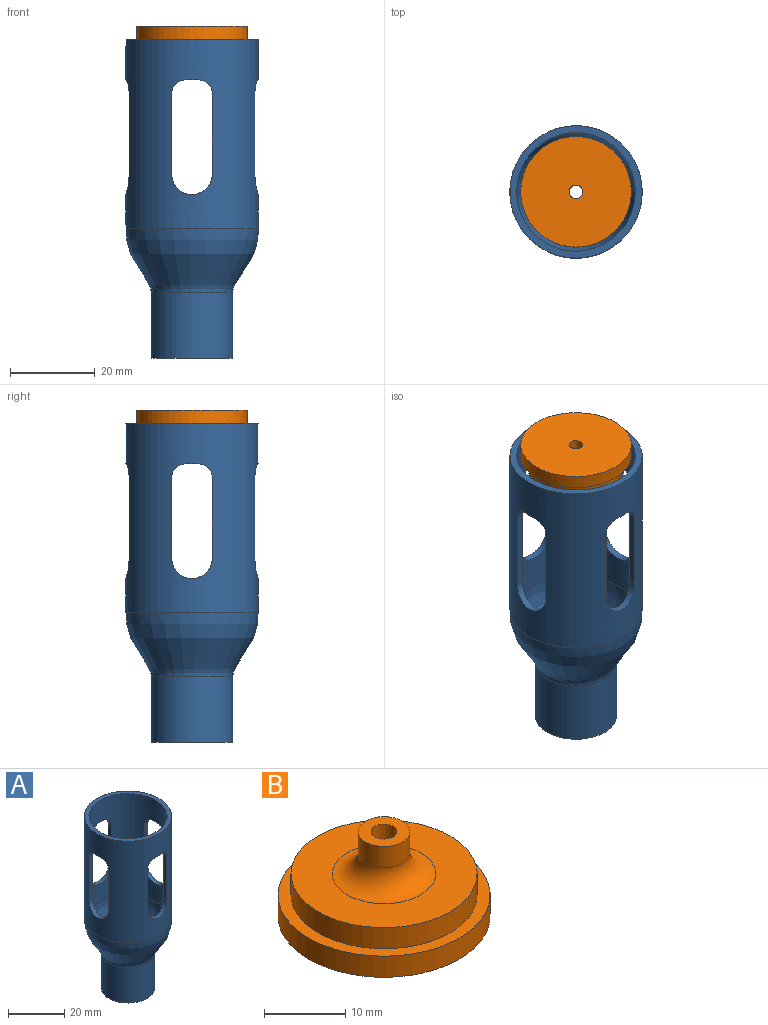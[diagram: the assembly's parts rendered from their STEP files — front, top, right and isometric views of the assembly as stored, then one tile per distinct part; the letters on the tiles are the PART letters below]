
ASSEMBLY  parts=2 mates=1
PART A: 32 faces, bbox 31.1x31.1x75 mm
  f0: cylinder r=13.97mm len=44.48mm, axis (0,0,1), area 2913.2mm2, adj f2,f7,f8,f9,f10,f11,f12,f13
  f1: cylinder r=15.56mm len=44.45mm, axis (0,0,1), area 3358.1mm2, adj f6,f7,f8,f9,f10,f11,f12,f13
  f2: revolved ~27.95x27.95mm, area 1193.1mm2, adj f0,f3
  f3: cylinder r=8mm len=16mm, axis (0,0,1), area 766mm2, adj f2,f4
  f4: plane 19.18x19.18mm, normal (0,0,-1), area 87.7mm2, adj f3,f5
  f5: cylinder r=9.59mm len=19.18mm, axis (0,0,1), area 923.1mm2, adj f4,f6
  f6: revolved ~31.13x31.13mm, area 1371.2mm2, adj f1,f5
  f7: plane 31.12x31.12mm, normal (0,0,1), area 147.3mm2, adj f0,f1
  f8: plane 3.18x1.68mm, normal (0,0,-1), area 5.1mm2, adj f0,f1,f9,f13
  f9: cylinder r=3.17mm len=3.18mm, axis (0,-1,0), area 8.2mm2, adj f0,f1,f8,f10
  f10: plane 19.05x1.68mm, normal (-1,0,0), area 32mm2, adj f0,f1,f9,f11
  f11: cylinder r=4.76mm len=9.53mm, axis (0,-1,0), area 24.4mm2, adj f0,f1,f10,f12
  f12: plane 19.05x1.68mm, normal (1,0,0), area 32mm2, adj f0,f1,f11,f13
  f13: cylinder r=3.17mm len=3.18mm, axis (0,-1,0), area 8.2mm2, adj f0,f1,f8,f12
  f14: cylinder r=3.17mm len=3.18mm, axis (0,-1,0), area 8.2mm2, adj f0,f1,f15,f19
  f15: plane 19.05x1.68mm, normal (1,0,0), area 32mm2, adj f0,f1,f14,f16
  f16: cylinder r=4.76mm len=9.53mm, axis (0,-1,0), area 24.4mm2, adj f0,f1,f15,f17
  f17: plane 19.05x1.68mm, normal (-1,0,0), area 32mm2, adj f0,f1,f16,f18
  f18: cylinder r=3.17mm len=3.18mm, axis (0,-1,0), area 8.2mm2, adj f0,f1,f17,f19
  f19: plane 3.18x1.68mm, normal (0,0,-1), area 5.1mm2, adj f0,f1,f14,f18
  f20: plane 3.18x1.68mm, normal (0,0,-1), area 5.1mm2, adj f0,f1,f21,f25
  f21: cylinder r=3.17mm len=3.18mm, axis (-1,0,0), area 8.2mm2, adj f0,f1,f20,f22
  f22: plane 19.05x1.68mm, normal (0,-1,0), area 32mm2, adj f0,f1,f21,f23
  f23: cylinder r=4.76mm len=9.53mm, axis (-1,0,0), area 24.4mm2, adj f0,f1,f22,f24
  f24: plane 19.05x1.68mm, normal (0,1,0), area 32mm2, adj f0,f1,f23,f25
  f25: cylinder r=3.17mm len=3.18mm, axis (-1,0,0), area 8.2mm2, adj f0,f1,f20,f24
  f26: cylinder r=3.17mm len=3.18mm, axis (-1,0,0), area 8.2mm2, adj f0,f1,f27,f31
  f27: plane 19.05x1.68mm, normal (0,1,0), area 32mm2, adj f0,f1,f26,f28
  f28: cylinder r=4.76mm len=9.53mm, axis (-1,0,0), area 24.4mm2, adj f0,f1,f27,f29
  f29: plane 19.05x1.68mm, normal (0,-1,0), area 32mm2, adj f0,f1,f28,f30
  f30: cylinder r=3.17mm len=3.18mm, axis (-1,0,0), area 8.2mm2, adj f0,f1,f29,f31
  f31: plane 3.18x1.68mm, normal (0,0,-1), area 5.1mm2, adj f0,f1,f26,f30
PART B: 9 faces, bbox 26x26x12.7 mm
  f0: cylinder r=13.02mm len=26.04mm, axis (0,0,-1), area 259.7mm2, adj f1,f2
  f1: plane 26.04x26.04mm, normal (0,0,1), area 121.9mm2, adj f0,f3
  f2: plane 26.04x26.04mm, normal (0,0,-1), area 524.4mm2, adj f0,f5
  f3: cylinder r=11.43mm len=22.86mm, axis (0,0,-1), area 228mm2, adj f1,f4
  f4: plane 22.86x22.86mm, normal (0,0,1), area 283.8mm2, adj f3,f8
  f5: cylinder r=1.59mm len=12.7mm, axis (0,0,-1), area 126.7mm2, adj f2,f7
  f6: cylinder r=3.17mm len=6.35mm, axis (0,0,-1), area 63.3mm2, adj f7,f8
  f7: plane 6.35x6.35mm, normal (0,0,1), area 23.8mm2, adj f5,f6
  f8: torus R=6.35mm, axis (0,0,1), area 135.6mm2, adj f4,f6
PLACE A at identity
PLACE B rot(axis=(1,0,0),180deg) t=(0,0,78.13)mm
MATE fastened B.f0 <-> A.f0  axis (0,0,-1) through (0,0,74.96)mm
